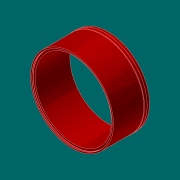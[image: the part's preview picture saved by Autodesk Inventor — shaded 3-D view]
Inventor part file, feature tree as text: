
AUTODESK INVENTOR PART (.ipt)
format: ipt  version: 2017.3 (Build 213257000, 257)  size: 145,408 bytes
history: native  units: in
note: dims shown in document units (in); Inventor stores cm internally (conversion verified against a paired STEP export)
features: extrude x4, sketch x4, chamfer x2, fillet x1
ambient origin geometry x8: Origin, YZ Plane, XZ Plane, XY Plane, X Axis, Y Axis, Z Axis, Center Point
bodies: Solid1 (feature_tree)
feature tree (11):
  extrude  "Extrusion1"  Depth=31.0in
  extrude  "Extrusion2"  Depth=12.9528in
  extrude  "Extrusion3"  Depth=1.0in
  chamfer  "Chamfer1"  Distance=1.0in
  extrude  "Extrusion4"  Depth=0.0312in TaperAngle=45.0deg
  fillet  "Fillet1"  Radius=29.98in
  chamfer  "Chamfer2"  Distance=0.5in
  sketch  "Sketch1"  dims[d0=28.5in d1=31.0in]
  sketch  "Sketch2"  dims[d2=12.9528in d3=0.0in d4=31.25in]
  sketch  "Sketch3"  dims[d5=2.0in d6=0.0in d7=30.98in d8=1.0in d9=0.0in]
  sketch  "Sketch4"  dims[d10=0.125in d11=0.125in d12=45.0deg d13=29.98in d14=0.5in d15=0.0in d16=0.0312in d17=0.0312in d18=0.125in d19=45.0deg]
